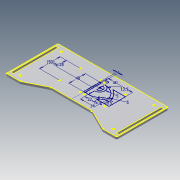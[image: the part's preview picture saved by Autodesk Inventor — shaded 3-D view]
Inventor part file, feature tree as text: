
AUTODESK INVENTOR PART (.ipt)
format: ipt  version: 2014 (Build 180170000, 170)  size: 201,216 bytes
history: native  units: mm
features: sketch x5, extrude x4, fillet x1
ambient origin geometry x8: Origin, YZ Plane, XZ Plane, XY Plane, X Axis, Y Axis, Z Axis, Center Point
bodies: Solid1 (feature_tree)
feature tree (10):
  extrude  "Extrusion1"  Depth=268.0mm
  extrude  "Extrusion2"  Depth=25.0mm
  extrude  "Extrusion5"  Depth=50.0mm
  fillet  "Fillet1"  Radius=3.0mm
  extrude  "Extrusion6"  Depth=21.5mm
  sketch  "Sketch9"  dims[d49=21.5mm d50=12.5mm d51=12.5mm d56=2.875mm d57=6.25mm d58=2.875mm d60=8.0mm d61=5.4mm d62=108.9mm d63=10.0mm d64=0.0mm d65=2.0mm d66=8.1mm d67=50.0mm d68=60.0mm d69=100.0mm d70=25.0mm d71=4.3mm d72=10.0mm d73=0.0mm d74=4.0mm d75=40.0mm d76=50.0mm d77=25.0mm d78=12.5mm d79=5.0mm d80=8.0mm d81=22.0mm d82=15.0mm d83=34.0mm d84=9.0mm d85=5.0mm d86=5.0mm d87=60.0mm]
  sketch  "Sketch1"  dims[d1=125.0mm d2=268.0mm]
  sketch  "Sketch2"  dims[d4=6.0mm d5=0.0mm d6=25.0mm]
  sketch  "Sketch7"  dims[d7=34.0mm d9=50.0mm d10=3.0mm d11=0.0mm]
  sketch  "Sketch8"  dims[d47=34.0mm d48=21.5mm]
